# Revit family: M_Valve_Balancing and Control_MEPcontent_Oventrop_Hydrocontrol VFR 10623
name_source: partatom
category: Pipe Accessories
revit_build: Autodesk Revit 2015 (Build: 20140223_1515(x64)
units: mm (PartAtom-declared; Revit-internal decimal feet)

## types (5) — shared parameters
Angle = 60.00°
Angle 2 = 30.00°
Angle 3 = -60.00°
Article Description = Balancing valve with flanges, PN 16
Article Type = Hydrocontrol VFR 10623
Black = Color RGB 35-35-35
Bronze = Color RGB 156-122-90
Content Supplier URL = www.mepcontent.eu
Custom = No
Description = Balancing valve with flanges, PN 16
EMCS Version = 2.0
ETIM Article Class = EC011463
Family Version = 10.14
Hb4 = 18 mm  [stored 0.0590551 ft]
Hb5 = 3 mm  [stored 0.00984252 ft]
Hlp1 = 22 mm  [stored 0.0721785 ft]
IFCExportAs = IfcValveType
IFCExportType = PRESSUREREDUCING
Lgt1 = 2 mm  [stored 0.00656168 ft]
MEPcontent Class = VALVE_BALANCING
Manufacturer = Oventrop
Manufacturer URL = http://www.oventrop.de
Model = Hydrocontrol VFR 10623
Pressure Drop = 0.0 Pa
Product Line = Oventrop
R1 = 9 mm  [stored 0.0295276 ft]
R2 = 10 mm  [stored 0.0328084 ft]
Revit Version = 2015
URL = www.stabiplan.com
r1 = 2 mm  [stored 0.00656168 ft]
r2 = 3 mm  [stored 0.00984252 ft]

## per-type parameters (varying)
- DN 65: CurDst=23 mm; Dst1=12 mm  [stored 0.0393701 ft]; DstChk=12 mm  [stored 0.0393701 ft]; FlangeDiameter=185 mm; GTIN=4026755251623; H=191 mm; Hb1=188 mm; Hb2=75 mm; Hb3=19 mm; Hb6=80 mm; Height=188 mm; Hlp2=8 mm  [stored 0.0262467 ft]; K=145 mm; L2=23 mm; Length=290 mm; Lgt2=16 mm  [stored 0.0524934 ft]; Lgt3=34 mm; Lgt4=110 mm; Manufacturer Art. No.=1062351; NominalDiameter=65 mm; NominalRadius=33 mm; OuterDiameter=76 mm; Rad1=73 mm; Rad2=93 mm; Rad3=43 mm; Rad4=40 mm  [stored 0.131234 ft]; Rad5=43 mm; Rad6=33 mm  [stored 0.108268 ft]; Rad7=45 mm; RegulatorRadius=55 mm  [stored 0.180446 ft]; VDst=29 mm; VHth=50 mm  [stored 0.164042 ft]
- DN 80: CurDst=28 mm  [stored 0.0918635 ft]; Dst1=13 mm; DstChk=13 mm; FlangeDiameter=200 mm; GTIN=4026755251630; H=206 mm; Hb1=206 mm; Hb2=88 mm; Hb3=22 mm  [stored 0.0721785 ft]; Hb6=95 mm; Height=203 mm; Hlp2=9 mm  [stored 0.0295276 ft]; K=160 mm; L2=28 mm  [stored 0.0918635 ft]; Length=310 mm; Lgt2=16 mm  [stored 0.0524934 ft]; Lgt3=37 mm; Lgt4=110 mm; Manufacturer Art. No.=1062352; NominalDiameter=80 mm; NominalRadius=40 mm; OuterDiameter=89 mm; Rad1=80 mm; Rad2=100 mm; Rad3=52 mm; Rad4=49 mm; Rad5=51 mm  [stored 0.167323 ft]; Rad6=41 mm; Rad7=53 mm  [stored 0.173885 ft]; RegulatorRadius=55 mm  [stored 0.180446 ft]; VDst=32 mm; VHth=59 mm
- DN 100: CurDst=34 mm; Dst1=11 mm  [stored 0.0360892 ft]; DstChk=11 mm  [stored 0.0360892 ft]; FlangeDiameter=220 mm; GTIN=4026755251647; H=243 mm; Hb1=234 mm; Hb2=110 mm; Hb3=27 mm  [stored 0.0885827 ft]; Hb6=120 mm; Height=240 mm; Hlp2=11 mm  [stored 0.0360892 ft]; K=180 mm; L2=34 mm; Length=350 mm; Lgt2=17 mm  [stored 0.0557743 ft]; Lgt3=41 mm; Lgt4=110 mm; Manufacturer Art. No.=1062353; NominalDiameter=100 mm; NominalRadius=50 mm; OuterDiameter=114 mm; Rad1=90 mm; Rad2=110 mm; Rad3=62 mm; Rad4=59 mm; Rad5=62 mm; Rad6=52 mm; Rad7=64 mm; RegulatorRadius=80 mm; VDst=36 mm; VHth=69 mm
- DN 125: CurDst=42 mm; Dst1=0 mm  [stored 0 ft]; DstChk=0 mm  [stored 0 ft]; FlangeDiameter=250 mm; GTIN=4026755251654; H=286 mm; Hb1=284 mm; Hb2=152 mm; Hb3=38 mm; Hb6=169 mm; Height=283 mm; Hlp2=14 mm  [stored 0.0459318 ft]; K=210 mm; L2=42 mm; Length=400 mm; Lgt2=18 mm  [stored 0.0590551 ft]; Lgt3=45 mm; Lgt4=158 mm; Manufacturer Art. No.=1062354; NominalDiameter=125 mm; NominalRadius=63 mm; OuterDiameter=140 mm; Rad1=105 mm; Rad2=125 mm; Rad3=76 mm; Rad4=73 mm; Rad5=75 mm; Rad6=65 mm  [stored 0.213255 ft]; Rad7=77 mm; RegulatorRadius=80 mm; VDst=40 mm  [stored 0.131234 ft]; VHth=83 mm
- DN 150: CurDst=50 mm  [stored 0.164042 ft]; Dst1=17 mm  [stored 0.0557743 ft]; DstChk=17 mm  [stored 0.0557743 ft]; FlangeDiameter=285 mm; GTIN=4026755251661; H=288 mm; Hb1=286 mm; Hb2=146 mm; Hb3=37 mm; Hb6=162 mm; Height=285 mm; Hlp2=17 mm  [stored 0.0557743 ft]; K=240 mm; L2=50 mm  [stored 0.164042 ft]; Length=480 mm; Lgt2=18 mm  [stored 0.0590551 ft]; Lgt3=50 mm  [stored 0.164042 ft]; Lgt4=205 mm; Manufacturer Art. No.=1062355; NominalDiameter=150 mm; NominalRadius=75 mm; OuterDiameter=168 mm; Rad1=120 mm; Rad2=143 mm; Rad3=89 mm; Rad4=86 mm; Rad5=89 mm; Rad6=79 mm; Rad7=91 mm; RegulatorRadius=80 mm; VDst=45 mm; VHth=96 mm

note: [stored X ft] marks values corroborated as IEEE doubles in the binary element streams (Revit-internal decimal feet)

## geometry (parser evidence)
native form markers: Blend x2, Sweep x2
no freeform markers — native parametric forms only
